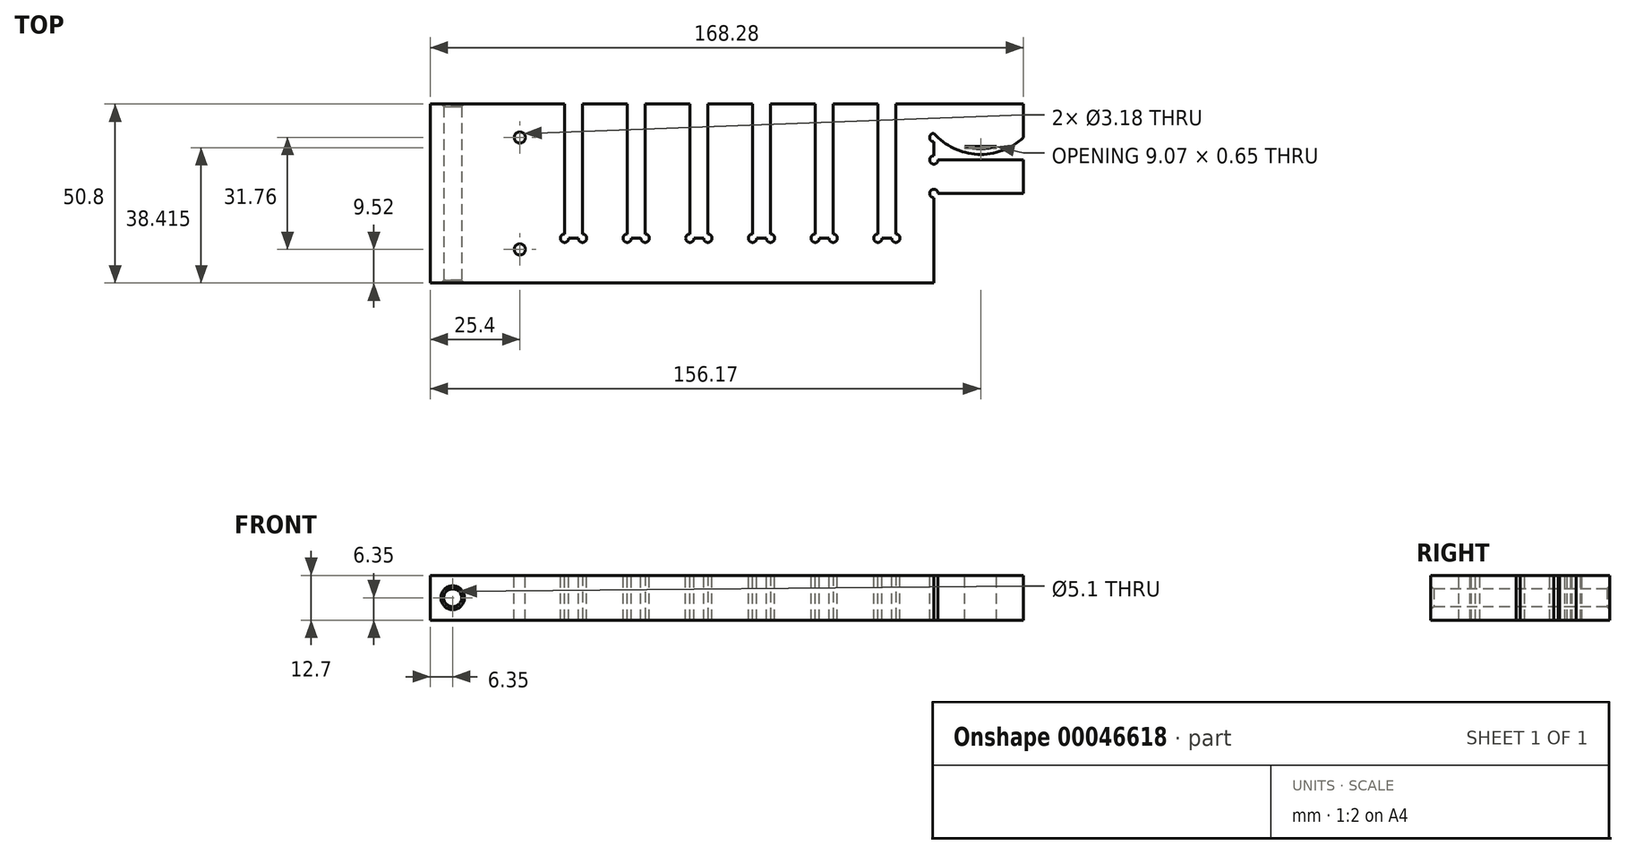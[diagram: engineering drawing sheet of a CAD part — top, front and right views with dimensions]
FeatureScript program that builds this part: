
annotation { "Feature Type Name" : "Feature", "Feature Type Description" : "" }
export const myFeature = defineFeature(function(context is Context, id is Id, definition is map)
    precondition{}
    {
        {
            var Q0;
            Q0=qCreatedBy(makeId("Top.planeOp"),FACE);
            var sketch = newSketch(context, id + "F10", { "sketchPlane" : qUnion([Q0])});
            skLineSegment(sketch, "E0.rect.bottom", {"start": v(-71.44, -25.4) * mm, "end": v(71.44, -25.4) * mm});
            skLineSegment(sketch, "E0.rect.top", {"start": v(-71.44, 25.4) * mm, "end": v(71.44, 25.4) * mm});
            skLineSegment(sketch, "E0.rect.left", {"start": v(-71.44, -25.4) * mm, "end": v(-71.44, 25.4) * mm});
            skLineSegment(sketch, "E0.rect.right", {"start": v(71.44, -25.4) * mm, "end": v(71.44, 25.4) * mm});
            skPoint(sketch, "E0.rect.middle", {"position": v(0, 0) * mm});
            skLineSegment(sketch, "E1.bottom", {"start": v(-71.44, -15.88) * mm, "end": v(-46.04, -15.88) * mm});
            skLineSegment(sketch, "E1.top", {"start": v(-71.44, 15.88) * mm, "end": v(-46.04, 15.88) * mm});
            skLineSegment(sketch, "E1.left", {"start": v(-71.44, -15.87) * mm, "end": v(-71.44, 15.88) * mm});
            skLineSegment(sketch, "E1.right", {"start": v(-46.04, -15.87) * mm, "end": v(-46.04, 15.88) * mm});
            skLineSegment(sketch, "E2.bottom", {"start": v(-33.34, 25.4) * mm, "end": v(-28.26, 25.4) * mm});
            skLineSegment(sketch, "E2.top", {"start": v(-33.34, -12.7) * mm, "end": v(-28.26, -12.7) * mm});
            skLineSegment(sketch, "E2.left", {"start": v(-33.34, 25.4) * mm, "end": v(-33.34, -12.7) * mm});
            skLineSegment(sketch, "E2.right", {"start": v(-28.26, 25.4) * mm, "end": v(-28.26, -12.7) * mm});
            skLineSegment(sketch, "E3.1.0.0", {"start": v(-15.56, 25.4) * mm, "end": v(-10.48, 25.4) * mm});
            skLineSegment(sketch, "E3.1.0.1", {"start": v(-15.56, 25.4) * mm, "end": v(-15.56, -12.7) * mm});
            skLineSegment(sketch, "E3.1.0.2", {"start": v(-10.48, 25.4) * mm, "end": v(-10.48, -12.7) * mm});
            skLineSegment(sketch, "E3.1.0.3", {"start": v(-15.56, -12.7) * mm, "end": v(-10.48, -12.7) * mm});
            skLineSegment(sketch, "E3.2.0.0", {"start": v(2.22, 25.4) * mm, "end": v(7.3, 25.4) * mm});
            skLineSegment(sketch, "E3.2.0.1", {"start": v(2.22, 25.4) * mm, "end": v(2.22, -12.7) * mm});
            skLineSegment(sketch, "E3.2.0.2", {"start": v(7.3, 25.4) * mm, "end": v(7.3, -12.7) * mm});
            skLineSegment(sketch, "E3.2.0.3", {"start": v(2.22, -12.7) * mm, "end": v(7.3, -12.7) * mm});
            skLineSegment(sketch, "E3.3.0.0", {"start": v(20, 25.4) * mm, "end": v(25.08, 25.4) * mm});
            skLineSegment(sketch, "E3.3.0.1", {"start": v(20, 25.4) * mm, "end": v(20, -12.7) * mm});
            skLineSegment(sketch, "E3.3.0.2", {"start": v(25.08, 25.4) * mm, "end": v(25.08, -12.7) * mm});
            skLineSegment(sketch, "E3.3.0.3", {"start": v(20, -12.7) * mm, "end": v(25.08, -12.7) * mm});
            skLineSegment(sketch, "E3.4.0.0", {"start": v(37.78, 25.4) * mm, "end": v(42.86, 25.4) * mm});
            skLineSegment(sketch, "E3.4.0.1", {"start": v(37.78, 25.4) * mm, "end": v(37.78, -12.7) * mm});
            skLineSegment(sketch, "E3.4.0.2", {"start": v(42.86, 25.4) * mm, "end": v(42.86, -12.7) * mm});
            skLineSegment(sketch, "E3.4.0.3", {"start": v(37.78, -12.7) * mm, "end": v(42.86, -12.7) * mm});
            skLineSegment(sketch, "E3.5.0.0", {"start": v(55.56, 25.4) * mm, "end": v(60.64, 25.4) * mm});
            skLineSegment(sketch, "E3.5.0.1", {"start": v(55.56, 25.4) * mm, "end": v(55.56, -12.7) * mm});
            skLineSegment(sketch, "E3.5.0.2", {"start": v(60.64, 25.4) * mm, "end": v(60.64, -12.7) * mm});
            skLineSegment(sketch, "E3.5.0.3", {"start": v(55.56, -12.7) * mm, "end": v(60.64, -12.7) * mm});
            skLineSegment(sketch, "E3.direction1", {"start": v(-33.34, 25.4) * mm, "end": v(-15.56, 25.4) * mm, "construction": true});
            skSolve(sketch);
        }
        {
            var Q0;
            {var subQ7=sQuery(id+"F10.wireOp",EDGE,"E0.rect.bottom");Q0=makeQuery(id+"F10.imprint","IMPRINT",FACE,{"disambiguationData":[TD([[makeQuery(id+"F10.imprint","IMPRINT",EDGE,{"derivedFrom":subQ7}),1.0]])]});}
            extrude(context, id + "F0", {"entities" : qUnion([Q0]), "depth" : 12.7 * mm});
        }
        {
            var Q0;
            Q0=makeQuery(id+"F0.opExtrude","SWEPT_FACE",FACE,{"disambiguationData":[OSD([sQuery(id+"F10.wireOp",EDGE,"E0.rect.bottom")])]});
            var sketch = newSketch(context, id + "F1", { "sketchPlane" : qUnion([Q0])});
            skCircle(sketch, "E4", {"center": v(-65.09, 6.35) * mm, "radius": 2.55 * mm});
            skPoint(sketch, "E4.centerSnap0", {"position": v(-71.44, 6.35) * mm});
            skSolve(sketch);
        }
        {
            var Q0;
            Q0=makeQuery(id+"F1.imprint","IMPRINT",FACE,{"disambiguationData":[TD([[makeQuery(id+"F1.imprint","IMPRINT",EDGE,{"derivedFrom":sQuery(id+"F1.wireOp",EDGE,"E4")}),1.0]])]});
            extrude(context, id + "F2", {"entities" : qUnion([Q0]), "operationType" : NewBodyOperationType.REMOVE, "endBound" : BoundingType.THROUGH_ALL, "oppositeDirection" : true, "depth" : 25.4 * mm});
        }
        {
            var Q0;
            Q0=makeQuery(id+"F2.boolean.opBoolean","COPY",FACE,{"derivedFrom":makeQuery(id+"F2.opExtrude","SWEPT_FACE",FACE,{"disambiguationData":[OSD([sQuery(id+"F1.wireOp",EDGE,"E4")])]})});
            chamfer(context, id + "F3", {"entities" : qUnion([Q0]), "width" : 0.8 * mm, "tangentPropagation" : true});
        }
        {
            var Q0;
            Q0=makeQuery(id+"F0.opExtrude","CAP_FACE",FACE,{"disambiguationData":[OSD([sQuery(id+"F10.wireOp",EDGE,"E0.rect.bottom"),sQuery(id+"F10.wireOp",EDGE,"E0.rect.top"),sQuery(id+"F10.wireOp",EDGE,"E0.rect.left"),sQuery(id+"F10.wireOp",EDGE,"E0.rect.right"),sQuery(id+"F10.wireOp",EDGE,"E1.bottom"),sQuery(id+"F10.wireOp",EDGE,"E1.top"),sQuery(id+"F10.wireOp",EDGE,"E1.right"),sQuery(id+"F10.wireOp",EDGE,"E2.top"),sQuery(id+"F10.wireOp",EDGE,"E2.left"),sQuery(id+"F10.wireOp",EDGE,"E2.right"),sQuery(id+"F10.wireOp",EDGE,"E3.1.0.1"),sQuery(id+"F10.wireOp",EDGE,"E3.1.0.2"),sQuery(id+"F10.wireOp",EDGE,"E3.1.0.3"),sQuery(id+"F10.wireOp",EDGE,"E3.2.0.1"),sQuery(id+"F10.wireOp",EDGE,"E3.2.0.2"),sQuery(id+"F10.wireOp",EDGE,"E3.2.0.3"),sQuery(id+"F10.wireOp",EDGE,"E3.3.0.1"),sQuery(id+"F10.wireOp",EDGE,"E3.3.0.2"),sQuery(id+"F10.wireOp",EDGE,"E3.3.0.3"),sQuery(id+"F10.wireOp",EDGE,"E3.4.0.1"),sQuery(id+"F10.wireOp",EDGE,"E3.4.0.2"),sQuery(id+"F10.wireOp",EDGE,"E3.4.0.3"),sQuery(id+"F10.wireOp",EDGE,"E3.5.0.1"),sQuery(id+"F10.wireOp",EDGE,"E3.5.0.2"),sQuery(id+"F10.wireOp",EDGE,"E3.5.0.3")])],"isStart":false});
            var sketch = newSketch(context, id + "F4", { "sketchPlane" : qUnion([Q0])});
            skCircle(sketch, "E5", {"center": v(-46.04, 15.88) * mm, "radius": 1.59 * mm});
            skCircle(sketch, "E6", {"center": v(-46.04, -15.88) * mm, "radius": 1.59 * mm});
            skCircle(sketch, "E7", {"center": v(-33.34, -12.7) * mm, "radius": 1.2 * mm});
            skCircle(sketch, "E8", {"center": v(-28.26, -12.7) * mm, "radius": 1.2 * mm});
            skCircle(sketch, "E9", {"center": v(-15.56, -12.7) * mm, "radius": 1.2 * mm});
            skCircle(sketch, "E10", {"center": v(-10.48, -12.7) * mm, "radius": 1.2 * mm});
            skCircle(sketch, "E11", {"center": v(2.22, -12.7) * mm, "radius": 1.2 * mm});
            skCircle(sketch, "E12", {"center": v(7.3, -12.7) * mm, "radius": 1.2 * mm});
            skCircle(sketch, "E13", {"center": v(20, -12.7) * mm, "radius": 1.2 * mm});
            skCircle(sketch, "E14", {"center": v(25.08, -12.7) * mm, "radius": 1.2 * mm});
            skCircle(sketch, "E15", {"center": v(37.78, -12.7) * mm, "radius": 1.2 * mm});
            skCircle(sketch, "E16", {"center": v(42.86, -12.7) * mm, "radius": 1.2 * mm});
            skCircle(sketch, "E17", {"center": v(55.56, -12.7) * mm, "radius": 1.2 * mm});
            skCircle(sketch, "E18", {"center": v(60.64, -12.7) * mm, "radius": 1.2 * mm});
            skSolve(sketch);
        }
        {
            var Q0;
            {var subQ1=sQuery(id+"F4.wireOp",EDGE,"E5");var subQ3=makeQuery(id+"F0.opExtrude","CAP_EDGE",EDGE,{"disambiguationData":[OSD([sQuery(id+"F10.wireOp",EDGE,"E1.top")])],"isStart":false});var subQ5=makeQuery(id+"F4.imprint","INTERSECT",VERTEX,{"derivedFrom":[subQ3,subQ1]});Q0=makeQuery(id+"F4.imprint","IMPRINT",FACE,{"disambiguationData":[TD([[makeQuery(id+"F4.imprint","IMPRINT",EDGE,{"disambiguationData":[TD([[subQ5,1.0]])],"derivedFrom":subQ1}),1.0]])]});}
            var Q1;
            {var subQ0=makeQuery(id+"F0.opExtrude","CAP_EDGE",EDGE,{"disambiguationData":[OSD([sQuery(id+"F10.wireOp",EDGE,"E1.bottom")])],"isStart":false});var subQ1=sQuery(id+"F4.wireOp",EDGE,"E6");var subQ2=makeQuery(id+"F4.imprint","INTERSECT",VERTEX,{"derivedFrom":[subQ0,subQ1]});Q1=makeQuery(id+"F4.imprint","IMPRINT",FACE,{"disambiguationData":[TD([[makeQuery(id+"F4.imprint","IMPRINT",EDGE,{"disambiguationData":[TD([[subQ2,-1.0]])],"derivedFrom":subQ1}),1.0]])]});}
            extrude(context, id + "F5", {"entities" : qUnion([Q0, Q1]), "operationType" : NewBodyOperationType.REMOVE, "endBound" : BoundingType.THROUGH_ALL, "oppositeDirection" : true, "depth" : 25.4 * mm});
        }
        {
            var Q0;
            {var subQ1=sQuery(id+"F4.wireOp",EDGE,"E7");var subQ3=makeQuery(id+"F0.opExtrude","CAP_EDGE",EDGE,{"disambiguationData":[OSD([sQuery(id+"F10.wireOp",EDGE,"E2.top")])],"isStart":false});var subQ5=makeQuery(id+"F4.imprint","INTERSECT",VERTEX,{"derivedFrom":[subQ3,subQ1]});Q0=makeQuery(id+"F4.imprint","IMPRINT",FACE,{"disambiguationData":[TD([[makeQuery(id+"F4.imprint","IMPRINT",EDGE,{"disambiguationData":[TD([[subQ5,1.0]])],"derivedFrom":subQ1}),1.0]])]});}
            var Q1;
            {var subQ1=sQuery(id+"F4.wireOp",EDGE,"E8");var subQ3=makeQuery(id+"F0.opExtrude","CAP_EDGE",EDGE,{"disambiguationData":[OSD([sQuery(id+"F10.wireOp",EDGE,"E2.top")])],"isStart":false});var subQ5=makeQuery(id+"F4.imprint","INTERSECT",VERTEX,{"derivedFrom":[subQ3,subQ1]});Q1=makeQuery(id+"F4.imprint","IMPRINT",FACE,{"disambiguationData":[TD([[makeQuery(id+"F4.imprint","IMPRINT",EDGE,{"disambiguationData":[TD([[subQ5,-1.0]])],"derivedFrom":subQ1}),1.0]])]});}
            var Q2;
            {var subQ1=sQuery(id+"F4.wireOp",EDGE,"E9");var subQ3=makeQuery(id+"F0.opExtrude","CAP_EDGE",EDGE,{"disambiguationData":[OSD([sQuery(id+"F10.wireOp",EDGE,"E3.1.0.1")])],"isStart":false});var subQ5=makeQuery(id+"F4.imprint","INTERSECT",VERTEX,{"derivedFrom":[subQ3,subQ1]});Q2=makeQuery(id+"F4.imprint","IMPRINT",FACE,{"disambiguationData":[TD([[makeQuery(id+"F4.imprint","IMPRINT",EDGE,{"disambiguationData":[TD([[subQ5,-1.0]])],"derivedFrom":subQ1}),1.0]])]});}
            var Q3;
            {var subQ1=sQuery(id+"F4.wireOp",EDGE,"E10");var subQ3=makeQuery(id+"F0.opExtrude","CAP_EDGE",EDGE,{"disambiguationData":[OSD([sQuery(id+"F10.wireOp",EDGE,"E3.1.0.2")])],"isStart":false});var subQ5=makeQuery(id+"F4.imprint","INTERSECT",VERTEX,{"derivedFrom":[subQ3,subQ1]});Q3=makeQuery(id+"F4.imprint","IMPRINT",FACE,{"disambiguationData":[TD([[makeQuery(id+"F4.imprint","IMPRINT",EDGE,{"disambiguationData":[TD([[subQ5,1.0]])],"derivedFrom":subQ1}),1.0]])]});}
            var Q4;
            {var subQ1=sQuery(id+"F4.wireOp",EDGE,"E11");var subQ3=makeQuery(id+"F0.opExtrude","CAP_EDGE",EDGE,{"disambiguationData":[OSD([sQuery(id+"F10.wireOp",EDGE,"E3.2.0.1")])],"isStart":false});var subQ5=makeQuery(id+"F4.imprint","INTERSECT",VERTEX,{"derivedFrom":[subQ3,subQ1]});Q4=makeQuery(id+"F4.imprint","IMPRINT",FACE,{"disambiguationData":[TD([[makeQuery(id+"F4.imprint","IMPRINT",EDGE,{"disambiguationData":[TD([[subQ5,-1.0]])],"derivedFrom":subQ1}),1.0]])]});}
            var Q5;
            {var subQ1=sQuery(id+"F4.wireOp",EDGE,"E12");var subQ3=makeQuery(id+"F0.opExtrude","CAP_EDGE",EDGE,{"disambiguationData":[OSD([sQuery(id+"F10.wireOp",EDGE,"E3.2.0.2")])],"isStart":false});var subQ5=makeQuery(id+"F4.imprint","INTERSECT",VERTEX,{"derivedFrom":[subQ3,subQ1]});Q5=makeQuery(id+"F4.imprint","IMPRINT",FACE,{"disambiguationData":[TD([[makeQuery(id+"F4.imprint","IMPRINT",EDGE,{"disambiguationData":[TD([[subQ5,1.0]])],"derivedFrom":subQ1}),1.0]])]});}
            var Q6;
            {var subQ1=sQuery(id+"F4.wireOp",EDGE,"E13");var subQ3=makeQuery(id+"F0.opExtrude","CAP_EDGE",EDGE,{"disambiguationData":[OSD([sQuery(id+"F10.wireOp",EDGE,"E3.3.0.1")])],"isStart":false});var subQ5=makeQuery(id+"F4.imprint","INTERSECT",VERTEX,{"derivedFrom":[subQ3,subQ1]});Q6=makeQuery(id+"F4.imprint","IMPRINT",FACE,{"disambiguationData":[TD([[makeQuery(id+"F4.imprint","IMPRINT",EDGE,{"disambiguationData":[TD([[subQ5,-1.0]])],"derivedFrom":subQ1}),1.0]])]});}
            var Q7;
            {var subQ1=sQuery(id+"F4.wireOp",EDGE,"E14");var subQ3=makeQuery(id+"F0.opExtrude","CAP_EDGE",EDGE,{"disambiguationData":[OSD([sQuery(id+"F10.wireOp",EDGE,"E3.3.0.2")])],"isStart":false});var subQ5=makeQuery(id+"F4.imprint","INTERSECT",VERTEX,{"derivedFrom":[subQ3,subQ1]});Q7=makeQuery(id+"F4.imprint","IMPRINT",FACE,{"disambiguationData":[TD([[makeQuery(id+"F4.imprint","IMPRINT",EDGE,{"disambiguationData":[TD([[subQ5,1.0]])],"derivedFrom":subQ1}),1.0]])]});}
            var Q8;
            {var subQ1=sQuery(id+"F4.wireOp",EDGE,"E15");var subQ3=makeQuery(id+"F0.opExtrude","CAP_EDGE",EDGE,{"disambiguationData":[OSD([sQuery(id+"F10.wireOp",EDGE,"E3.4.0.1")])],"isStart":false});var subQ5=makeQuery(id+"F4.imprint","INTERSECT",VERTEX,{"derivedFrom":[subQ3,subQ1]});Q8=makeQuery(id+"F4.imprint","IMPRINT",FACE,{"disambiguationData":[TD([[makeQuery(id+"F4.imprint","IMPRINT",EDGE,{"disambiguationData":[TD([[subQ5,-1.0]])],"derivedFrom":subQ1}),1.0]])]});}
            var Q9;
            {var subQ1=sQuery(id+"F4.wireOp",EDGE,"E16");var subQ3=makeQuery(id+"F0.opExtrude","CAP_EDGE",EDGE,{"disambiguationData":[OSD([sQuery(id+"F10.wireOp",EDGE,"E3.4.0.2")])],"isStart":false});var subQ5=makeQuery(id+"F4.imprint","INTERSECT",VERTEX,{"derivedFrom":[subQ3,subQ1]});Q9=makeQuery(id+"F4.imprint","IMPRINT",FACE,{"disambiguationData":[TD([[makeQuery(id+"F4.imprint","IMPRINT",EDGE,{"disambiguationData":[TD([[subQ5,1.0]])],"derivedFrom":subQ1}),1.0]])]});}
            var Q10;
            {var subQ0=makeQuery(id+"F0.opExtrude","CAP_EDGE",EDGE,{"disambiguationData":[OSD([sQuery(id+"F10.wireOp",EDGE,"E3.5.0.1")])],"isStart":false});var subQ1=sQuery(id+"F4.wireOp",EDGE,"E17");var subQ2=makeQuery(id+"F4.imprint","INTERSECT",VERTEX,{"derivedFrom":[subQ0,subQ1]});Q10=makeQuery(id+"F4.imprint","IMPRINT",FACE,{"disambiguationData":[TD([[makeQuery(id+"F4.imprint","IMPRINT",EDGE,{"disambiguationData":[TD([[subQ2,-1.0]])],"derivedFrom":subQ1}),1.0]])]});}
            var Q11;
            {var subQ1=sQuery(id+"F4.wireOp",EDGE,"E18");var subQ3=makeQuery(id+"F0.opExtrude","CAP_EDGE",EDGE,{"disambiguationData":[OSD([sQuery(id+"F10.wireOp",EDGE,"E3.5.0.2")])],"isStart":false});var subQ5=makeQuery(id+"F4.imprint","INTERSECT",VERTEX,{"derivedFrom":[subQ3,subQ1]});Q11=makeQuery(id+"F4.imprint","IMPRINT",FACE,{"disambiguationData":[TD([[makeQuery(id+"F4.imprint","IMPRINT",EDGE,{"disambiguationData":[TD([[subQ5,1.0]])],"derivedFrom":subQ1}),1.0]])]});}
            extrude(context, id + "F6", {"entities" : qUnion([Q0, Q1, Q2, Q3, Q4, Q5, Q6, Q7, Q8, Q9, Q10, Q11]), "operationType" : NewBodyOperationType.REMOVE, "endBound" : BoundingType.UP_TO_NEXT, "oppositeDirection" : true, "depth" : 25.4 * mm});
        }
        {
            var Q0;
            Q0=makeQuery(id+"F0.opExtrude","SWEPT_FACE",FACE,{"disambiguationData":[OSD([sQuery(id+"F10.wireOp",EDGE,"E0.rect.right")])]});
            var sketch = newSketch(context, id + "F7", { "sketchPlane" : qUnion([Q0])});
            skLineSegment(sketch, "E19.bottom", {"start": v(25.4, 12.7) * mm, "end": v(0, 12.7) * mm});
            skLineSegment(sketch, "E19.top", {"start": v(25.4, 0) * mm, "end": v(0, 0) * mm});
            skLineSegment(sketch, "E19.left", {"start": v(25.4, 12.7) * mm, "end": v(25.4, 0) * mm});
            skLineSegment(sketch, "E19.right", {"start": v(0, 12.7) * mm, "end": v(0, 0) * mm});
            skSolve(sketch);
        }
        {
            var Q0;
            Q0=makeQuery(id+"F7.imprint","IMPRINT",FACE,{"disambiguationData":[TD([[makeQuery(id+"F7.imprint","IMPRINT",EDGE,{"derivedFrom":sQuery(id+"F7.wireOp",EDGE,"E19.bottom")}),-1.0]])]});
            extrude(context, id + "F8", {"entities" : qUnion([Q0]), "operationType" : NewBodyOperationType.ADD, "depth" : 25.4 * mm});
        }
        {
            var Q0;
            Q0=makeQuery(id+"F8.boolean.opBoolean","MERGE",FACE,{"derivedFrom":[makeQuery(id+"F0.opExtrude","CAP_FACE",FACE,{"disambiguationData":[OSD([sQuery(id+"F10.wireOp",EDGE,"E0.rect.bottom"),sQuery(id+"F10.wireOp",EDGE,"E0.rect.top"),sQuery(id+"F10.wireOp",EDGE,"E0.rect.left"),sQuery(id+"F10.wireOp",EDGE,"E0.rect.right"),sQuery(id+"F10.wireOp",EDGE,"E1.bottom"),sQuery(id+"F10.wireOp",EDGE,"E1.top"),sQuery(id+"F10.wireOp",EDGE,"E1.right"),sQuery(id+"F10.wireOp",EDGE,"E2.top"),sQuery(id+"F10.wireOp",EDGE,"E2.left"),sQuery(id+"F10.wireOp",EDGE,"E2.right"),sQuery(id+"F10.wireOp",EDGE,"E3.1.0.1"),sQuery(id+"F10.wireOp",EDGE,"E3.1.0.2"),sQuery(id+"F10.wireOp",EDGE,"E3.1.0.3"),sQuery(id+"F10.wireOp",EDGE,"E3.2.0.1"),sQuery(id+"F10.wireOp",EDGE,"E3.2.0.2"),sQuery(id+"F10.wireOp",EDGE,"E3.2.0.3"),sQuery(id+"F10.wireOp",EDGE,"E3.3.0.1"),sQuery(id+"F10.wireOp",EDGE,"E3.3.0.2"),sQuery(id+"F10.wireOp",EDGE,"E3.3.0.3"),sQuery(id+"F10.wireOp",EDGE,"E3.4.0.1"),sQuery(id+"F10.wireOp",EDGE,"E3.4.0.2"),sQuery(id+"F10.wireOp",EDGE,"E3.4.0.3"),sQuery(id+"F10.wireOp",EDGE,"E3.5.0.1"),sQuery(id+"F10.wireOp",EDGE,"E3.5.0.2"),sQuery(id+"F10.wireOp",EDGE,"E3.5.0.3")])],"isStart":false}),makeQuery(id+"F8.opExtrude","SWEPT_FACE",FACE,{"disambiguationData":[OSD([sQuery(id+"F7.wireOp",EDGE,"E19.bottom")])]})]});
            var sketch = newSketch(context, id + "F11", { "sketchPlane" : qUnion([Q0])});
            skLineSegment(sketch, "E20.rect.bottom", {"start": v(71.44, 9.53) * mm, "end": v(122.24, 9.53) * mm});
            skLineSegment(sketch, "E20.rect.top", {"start": v(71.44, 15.88) * mm, "end": v(122.24, 15.88) * mm});
            skLineSegment(sketch, "E20.rect.left", {"start": v(71.44, 9.53) * mm, "end": v(71.44, 15.88) * mm});
            skLineSegment(sketch, "E20.rect.right", {"start": v(122.24, 9.53) * mm, "end": v(122.24, 15.88) * mm});
            skPoint(sketch, "E20.rect.middle", {"position": v(96.84, 12.7) * mm});
            skLineSegment(sketch, "E21", {"start": v(71.44, 11.11) * mm, "end": v(96.84, 11.11) * mm, "construction": true});
            skPoint(sketch, "E22.first.point", {"position": v(84.14, 11.11) * mm});
            skPoint(sketch, "E22.second.point", {"position": v(96.84, 15.88) * mm});
            skLineSegment(sketch, "E23", {"start": v(71.44, 13.34) * mm, "end": v(96.84, 13.34) * mm});
            skCircle(sketch, "E24", {"center": v(71.44, 9.53) * mm, "radius": 1.2 * mm});
            skCircle(sketch, "E25", {"center": v(71.44, 0) * mm, "radius": 1.2 * mm});
            skCircle(sketch, "E26", {"center": v(71.44, 15.88) * mm, "radius": 1.2 * mm});
            skCircle(sketch, "E27", {"center": v(84.73, 28.84) * mm, "radius": 17.74 * mm});
            skPoint(sketch, "E27.second.point", {"position": v(72.63, 15.88) * mm});
            skCircle(sketch, "E28", {"center": v(84.73, 28.84) * mm, "radius": 16.15 * mm});
            skSolve(sketch);
        }
        {
            var Q0;
            {var subQ1=sQuery(id+"F11.wireOp",EDGE,"899d32b8-0a77-4b24-bed6-420299b2ceb6");var subQ4=sQuery(id+"F11.wireOp",EDGE,"E20.rect.top");var subQ6=makeQuery(id+"F11.imprint","INTERSECT",VERTEX,{"disambiguationData":[OD(0.0)],"derivedFrom":[subQ4,subQ1]});Q0=makeQuery(id+"F11.imprint","IMPRINT",FACE,{"disambiguationData":[TD([[makeQuery(id+"F11.imprint","IMPRINT",EDGE,{"disambiguationData":[TD([[subQ6,-1.0]])],"derivedFrom":subQ4}),-1.0]])]});}
            var Q1;
            {var subQ0=sQuery(id+"F11.wireOp",EDGE,"E23");var subQ1=sQuery(id+"F11.wireOp",EDGE,"899d32b8-0a77-4b24-bed6-420299b2ceb6");var subQ3=makeQuery(id+"F11.imprint","INTERSECT",VERTEX,{"disambiguationData":[OD(0.0)],"derivedFrom":[subQ1,subQ0]});Q1=makeQuery(id+"F11.imprint","IMPRINT",FACE,{"disambiguationData":[TD([[makeQuery(id+"F11.imprint","IMPRINT",EDGE,{"disambiguationData":[TD([[subQ3,-1.0]])],"derivedFrom":subQ1}),1.0]])]});}
            var Q2;
            {var subQ1=sQuery(id+"F11.wireOp",EDGE,"E20.rect.bottom");var subQ7=sQuery(id+"F11.wireOp",EDGE,"E20.rect.left");var subQ8=makeQuery(id+"F11.imprint","INTERSECT",VERTEX,{"derivedFrom":[subQ1,subQ7]});Q2=makeQuery(id+"F11.imprint","IMPRINT",FACE,{"disambiguationData":[TD([[makeQuery(id+"F11.imprint","IMPRINT",EDGE,{"disambiguationData":[TD([[subQ8,-1.0]])],"derivedFrom":subQ1}),1.0]])]});}
            var Q3;
            {var subQ0=sQuery(id+"F11.wireOp",EDGE,"E23");var subQ3=sQuery(id+"F11.wireOp",EDGE,"E20.rect.left");var subQ4=makeQuery(id+"F11.imprint","INTERSECT",VERTEX,{"derivedFrom":[subQ3,subQ0]});Q3=makeQuery(id+"F11.imprint","IMPRINT",FACE,{"disambiguationData":[TD([[makeQuery(id+"F11.imprint","IMPRINT",EDGE,{"disambiguationData":[TD([[subQ4,-1.0]])],"derivedFrom":subQ0}),1.0]])]});}
            var Q4;
            {var subQ0=makeQuery(id+"F8.opExtrude","CAP_EDGE",EDGE,{"disambiguationData":[OSD([sQuery(id+"F7.wireOp",EDGE,"E19.bottom")])],"isStart":false});var subQ3=sQuery(id+"F11.wireOp",EDGE,"E23");var subQ4=makeQuery(id+"F11.imprint","INTERSECT",VERTEX,{"derivedFrom":[subQ0,subQ3]});Q4=makeQuery(id+"F11.imprint","IMPRINT",FACE,{"disambiguationData":[TD([[makeQuery(id+"F11.imprint","IMPRINT",EDGE,{"disambiguationData":[TD([[subQ4,1.0]])],"derivedFrom":subQ3}),1.0]])]});}
            var Q5;
            {var subQ1=sQuery(id+"F11.wireOp",EDGE,"E20.rect.left");var subQ3=sQuery(id+"F11.wireOp",EDGE,"E20.rect.bottom");var subQ5=makeQuery(id+"F11.imprint","INTERSECT",VERTEX,{"derivedFrom":[subQ3,subQ1]});Q5=makeQuery(id+"F11.imprint","IMPRINT",FACE,{"disambiguationData":[TD([[makeQuery(id+"F11.imprint","IMPRINT",EDGE,{"disambiguationData":[TD([[subQ5,-1.0]])],"derivedFrom":subQ3}),-1.0]])]});}
            var Q6;
            {var subQ1=sQuery(id+"F11.wireOp",EDGE,"E20.rect.bottom");var subQ5=sQuery(id+"F11.wireOp",EDGE,"E24");var subQ8=makeQuery(id+"F11.imprint","INTERSECT",VERTEX,{"derivedFrom":[subQ1,subQ5]});Q6=makeQuery(id+"F11.imprint","IMPRINT",FACE,{"disambiguationData":[TD([[makeQuery(id+"F11.imprint","IMPRINT",EDGE,{"disambiguationData":[TD([[subQ8,-1.0]])],"derivedFrom":subQ1}),1.0]])]});}
            var Q7;
            {var subQ0=sQuery(id+"F10.wireOp",EDGE,"E0.rect.right");var subQ1=makeQuery(id+"F0.opExtrude","CAP_EDGE",EDGE,{"disambiguationData":[OSD([subQ0])],"isStart":false});var subQ2=sQuery(id+"F11.wireOp",EDGE,"E25");var subQ3=makeQuery(id+"F11.imprint","INTERSECT",VERTEX,{"derivedFrom":[subQ1,subQ2]});Q7=makeQuery(id+"F11.imprint","IMPRINT",FACE,{"disambiguationData":[TD([[makeQuery(id+"F11.imprint","IMPRINT",EDGE,{"disambiguationData":[TD([[subQ3,1.0]])],"derivedFrom":subQ2}),1.0]])]});}
            var Q8;
            {var subQ1=sQuery(id+"F11.wireOp",EDGE,"E20.rect.top");var subQ3=sQuery(id+"F11.wireOp",EDGE,"E20.rect.left");var subQ5=makeQuery(id+"F11.imprint","INTERSECT",VERTEX,{"derivedFrom":[subQ1,subQ3]});Q8=makeQuery(id+"F11.imprint","IMPRINT",FACE,{"disambiguationData":[TD([[makeQuery(id+"F11.imprint","IMPRINT",EDGE,{"disambiguationData":[TD([[subQ5,1.0]])],"derivedFrom":subQ3}),-1.0]])]});}
            var Q9;
            {var subQ1=sQuery(id+"F11.wireOp",EDGE,"E20.rect.top");var subQ5=sQuery(id+"F11.wireOp",EDGE,"E20.rect.left");var subQ7=makeQuery(id+"F11.imprint","INTERSECT",VERTEX,{"derivedFrom":[subQ1,subQ5]});Q9=makeQuery(id+"F11.imprint","IMPRINT",FACE,{"disambiguationData":[TD([[makeQuery(id+"F11.imprint","IMPRINT",EDGE,{"disambiguationData":[TD([[subQ7,1.0]])],"derivedFrom":subQ5}),1.0]])]});}
            var Q10;
            {var subQ0=sQuery(id+"F11.wireOp",EDGE,"E28");var subQ1=sQuery(id+"F11.wireOp",EDGE,"E23");var subQ3=makeQuery(id+"F11.imprint","INTERSECT",VERTEX,{"disambiguationData":[OD(0.0)],"derivedFrom":[subQ1,subQ0]});Q10=makeQuery(id+"F11.imprint","IMPRINT",FACE,{"disambiguationData":[TD([[makeQuery(id+"F11.imprint","IMPRINT",EDGE,{"disambiguationData":[TD([[subQ3,-1.0]])],"derivedFrom":subQ1}),-1.0]])]});}
            extrude(context, id + "F9", {"entities" : qUnion([Q0, Q1, Q2, Q3, Q4, Q5, Q6, Q7, Q8, Q9, Q10]), "operationType" : NewBodyOperationType.REMOVE, "endBound" : BoundingType.UP_TO_NEXT, "oppositeDirection" : true, "depth" : 25.4 * mm});
        }
    });
